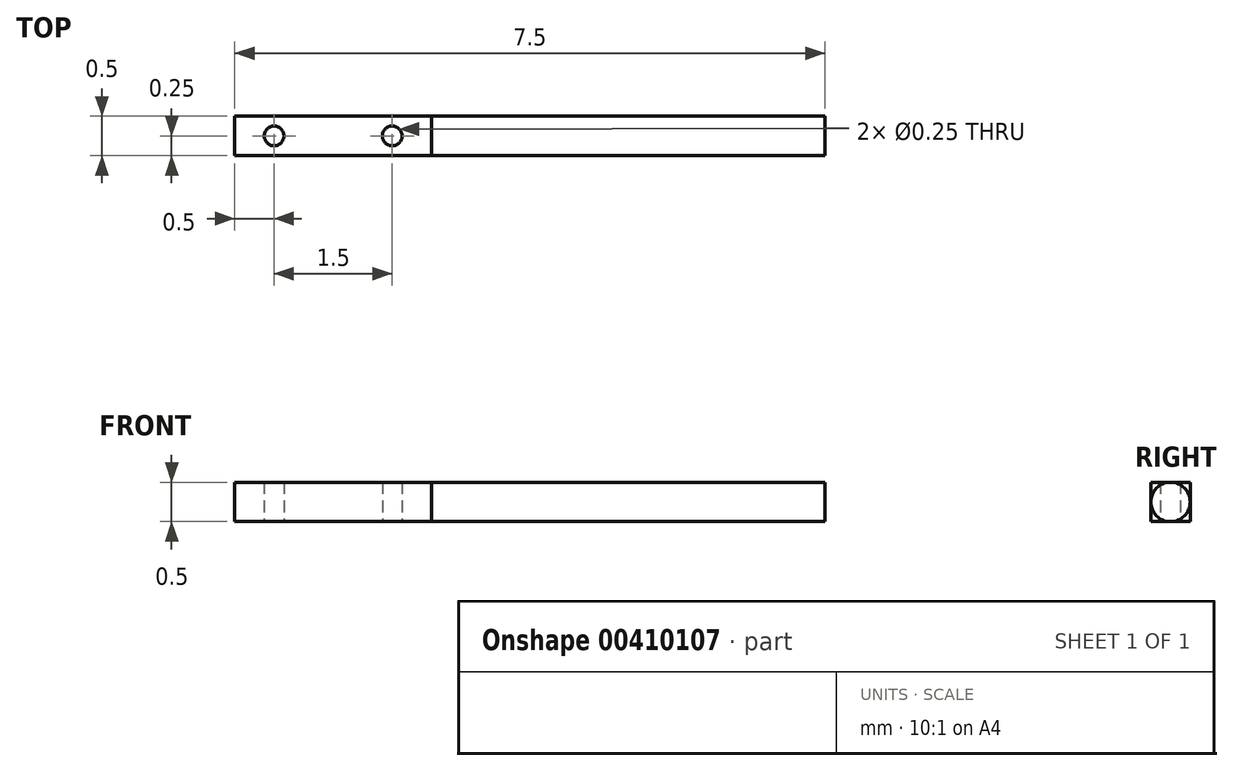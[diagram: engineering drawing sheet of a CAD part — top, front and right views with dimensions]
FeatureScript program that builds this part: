
annotation { "Feature Type Name" : "Feature", "Feature Type Description" : "" }
export const myFeature = defineFeature(function(context is Context, id is Id, definition is map)
    precondition{}
    {
        {
            var Q0;
            Q0=qCreatedBy(makeId("Top.planeOp"),FACE);
            var sketch = newSketch(context, id + "F0", { "sketchPlane" : qUnion([Q0])});
            skLineSegment(sketch, "E0.bottom", {"start": v(0, 0.5) * mm, "end": v(2.5, 0.5) * mm});
            skLineSegment(sketch, "E0.top", {"start": v(0, 0) * mm, "end": v(2.5, 0) * mm});
            skLineSegment(sketch, "E0.left", {"start": v(0, 0.5) * mm, "end": v(0, 0) * mm});
            skLineSegment(sketch, "E0.right", {"start": v(2.5, 0.5) * mm, "end": v(2.5, 0) * mm});
            skCircle(sketch, "E1", {"center": v(0.5, 0.25) * mm, "radius": 0.12 * mm});
            skPoint(sketch, "E1.centerSnap0", {"position": v(0, 0.25) * mm});
            skCircle(sketch, "E2", {"center": v(2, 0.25) * mm, "radius": 0.12 * mm});
            skSolve(sketch);
        }
        {
            var Q0;
            Q0 = qSketchRegion(id + "F0", true);
            extrude(context, id + "F1", {"entities" : qUnion([Q0]), "depth" : 0.5 * mm});
        }
        {
            var Q0;
            Q0=makeQuery(id+"F1.opExtrude","SWEPT_FACE",FACE,{"disambiguationData":[OSD([sQuery(id+"F0.wireOp",EDGE,"E0.right")])]});
            var sketch = newSketch(context, id + "F2", { "sketchPlane" : qUnion([Q0])});
            skCircle(sketch, "E3", {"center": v(0.25, 0.25) * mm, "radius": 0.25 * mm});
            skPoint(sketch, "E3.centerSnap0", {"position": v(0.5, 0.25) * mm});
            skPoint(sketch, "E3.centerSnap1", {"position": v(0.25, 0) * mm});
            skSolve(sketch);
        }
        {
            var Q0;
            Q0 = qSketchRegion(id + "F2", true);
            extrude(context, id + "F3", {"entities" : qUnion([Q0]), "operationType" : NewBodyOperationType.ADD, "depth" : 5 * mm});
        }
    });
